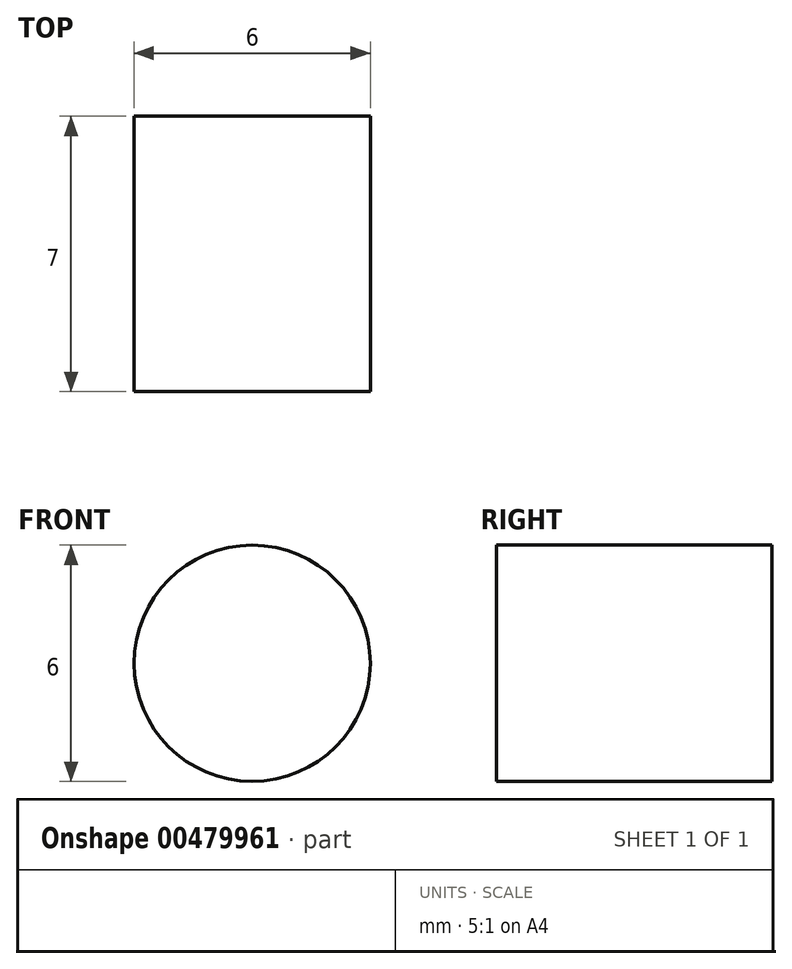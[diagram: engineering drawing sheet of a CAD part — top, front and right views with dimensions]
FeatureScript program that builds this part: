
annotation { "Feature Type Name" : "Feature", "Feature Type Description" : "" }
export const myFeature = defineFeature(function(context is Context, id is Id, definition is map)
    precondition{}
    {
        {
            var Q0;
            Q0=qCreatedBy(makeId("Front.planeOp"),FACE);
            var sketch = newSketch(context, id + "F0", { "sketchPlane" : qUnion([Q0])});
            skCircle(sketch, "E0", {"center": v(0, 0) * mm, "radius": 3 * mm});
            skSolve(sketch);
        }
        {
            var Q0;
            Q0=makeQuery(id+"F0.imprint","IMPRINT",FACE,{"disambiguationData":[TD([[makeQuery(id+"F0.imprint","IMPRINT",EDGE,{"derivedFrom":sQuery(id+"F0.wireOp",EDGE,"E0")}),1.0]])]});
            extrude(context, id + "F1", {"entities" : qUnion([Q0]), "depth" : 7 * mm});
        }
    });
